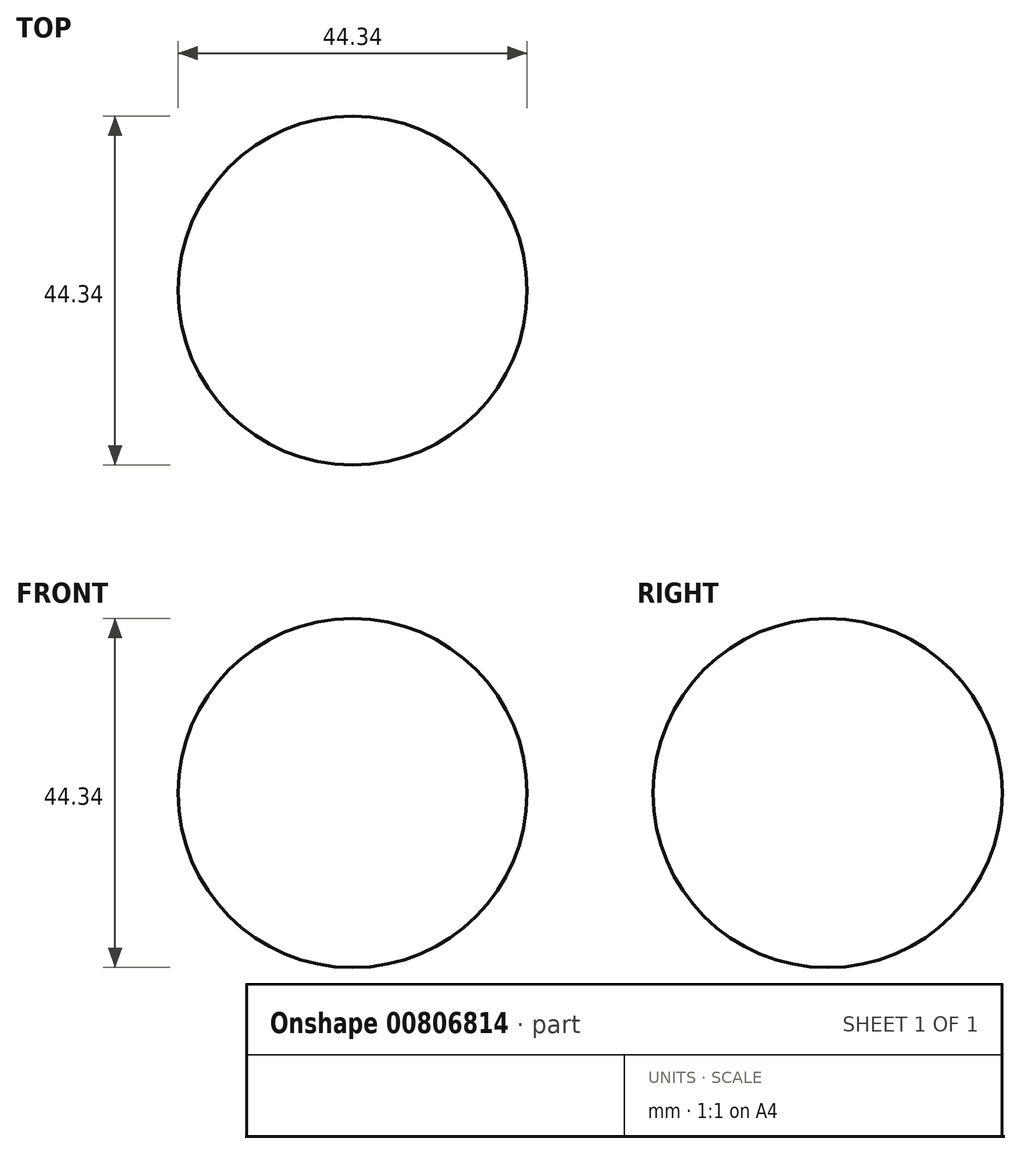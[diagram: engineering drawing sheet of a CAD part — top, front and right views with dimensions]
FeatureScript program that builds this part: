
annotation { "Feature Type Name" : "Feature", "Feature Type Description" : "" }
export const myFeature = defineFeature(function(context is Context, id is Id, definition is map)
    precondition{}
    {
        {
            var Q0;
            Q0=qCreatedBy(makeId("Front.planeOp"),FACE);
            var sketch = newSketch(context, id + "F0", { "sketchPlane" : qUnion([Q0])});
            skCircle(sketch, "E0", {"center": v(0, 0) * mm, "radius": 22.17 * mm});
            skLineSegment(sketch, "E1", {"start": v(0, -46.62) * mm, "end": v(0, 41.67) * mm});
            skSolve(sketch);
        }
        {
            var Q0;
            {var subQ0=sQuery(id+"F0.wireOp",EDGE,"E1");var subQ1=sQuery(id+"F0.wireOp",EDGE,"E0");var subQ2=makeQuery(id+"F0.imprint","INTERSECT",VERTEX,{"disambiguationData":[OD(0.0)],"derivedFrom":[subQ1,subQ0]});Q0=makeQuery(id+"F0.imprint","IMPRINT",FACE,{"disambiguationData":[TD([[makeQuery(id+"F0.imprint","IMPRINT",EDGE,{"disambiguationData":[TD([[subQ2,1.0]])],"derivedFrom":subQ1}),1.0]])]});}
            var Q1;
            Q1=sQuery(id+"F0.wireOp",EDGE,"E1");
            revolve(context, id + "F1", {"surfaceOperationType" : NewSurfaceOperationType.NEW, "entities" : qUnion([Q0]), "axis" : qUnion([Q1]), "revolveType" : RevolveType.FULL});
        }
    });
